# Revit family: RollHolder-WithCover-Vitra-OriginSeries-A44888
name_source: partatom
category: Plumbing Fixtures
revit_build: Autodesk Revit 2017 (Build: 20160225_1515(x64)
units: mm (PartAtom-declared; Revit-internal decimal feet)

## family parameters
Cut with Voids When Loaded = No
Host = Face
OmniClass Number = 23.45.00.00
OmniClass Title = Sanitary, Laundry, and Cleaning Equipment
Part Type = Normal
Room Calculation Point = No
Round Connector Dimension = Use Diameter
Shared = Yes

## types (4) — shared parameters
BIMobject category = Sanitary - Bathroom Accessories
Brand = VitrA
CW Connection = No
Default Elevation = 600 mm
Description = Origin Roll Holder
Design country = Turkey
HW Connection = No
IFC Classification = Sanitary Terminal
Main Material = Metal
Manufacturer = Vitra
Manufacturer name = Vitra
Mounting type = Wall Mounted
NBS Referans Code = 35-75-88
NBS Referans Description = Toilet Roll Holders
Nominal Depth (mm) = 130 mm  [stored 0.426509 ft]
Nominal Height (mm) = 140 mm  [stored 0.459318 ft]
Nominal Width (mm) = 100 mm  [stored 0.328084 ft]
OmniClass Code = 23-31 25 00
OmniClass Description = Toilet and Bath Specialties
Product Type = Built-in Roll Holder
Product certification = https://www.vitraglobal.com
Product family = OriginSeries
Product group = Roll Holder
Product url = https://vitraglobal.com
Technical description = https://vitraglobal.com
URL = https://vitraglobal.com
Uniclass 1.4 Code = L7313
Uniclass 1.4 Description = Sanitary above ground pipes and fittings
Uniclass 2.0 Code = PR-35-75-88
Uniclass 2.0 Description = Toilet Roll Holders
Uniclass 2015 Code = Pr_40_20_76_88
Uniclass 2015 Name = Toilet roll holders
Uniformat II Description = FURNISHINGS
Vent Connection = No
Warranty Period (Year) = 5 years
Waste Connection = No
Weight Net (kg) = 0.8
Youtube = https://www.youtube.com

## per-type parameters (varying)
| type | Article No. (default) | Coating Material | Color | Model | Product SKU | Product data url |
| RollHolder-Vitra-OriginSeries-(Chrome)-A44888 | A44888 | Chrome | Chrome | A44888 | A44888 | https://www.bimobject.com |
| RollHolder-Vitra-OriginSeries-(Black)-A4488836 | A4488836 | Black | Black | A4488836 | A4488836 |  |
| RollHolder-Vitra-OriginSeries-(BrushedNickel)-A4488834 | A4488834 | Brushed Nickel | Brushed Nickel | A4488834 | A4488834 |  |
| RollHolder-Vitra-OriginSeries-(Copper)-A4488826 | A4488826 | Copper | Copper | A4488826 | A4488826 |  |

note: [stored X ft] marks values corroborated as IEEE doubles in the binary element streams (Revit-internal decimal feet)

## geometry (parser evidence)
native form markers: Sweep x3
no freeform markers — native parametric forms only
